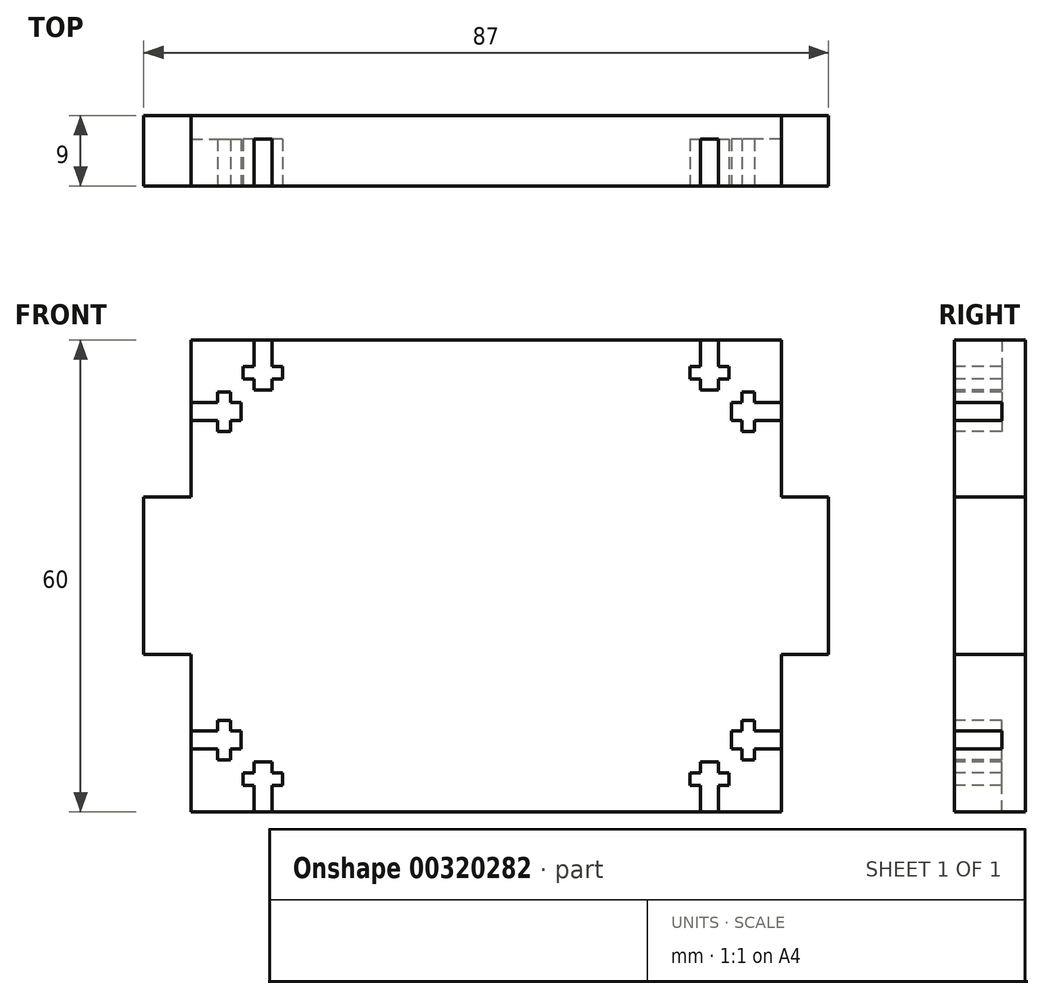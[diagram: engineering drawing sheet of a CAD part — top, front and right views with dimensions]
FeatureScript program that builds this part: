
annotation { "Feature Type Name" : "Feature", "Feature Type Description" : "" }
export const myFeature = defineFeature(function(context is Context, id is Id, definition is map)
    precondition{}
    {
        {
            var Q0;
            Q0=qCreatedBy(makeId("Front.planeOp"),FACE);
            var sketch = newSketch(context, id + "F0", { "sketchPlane" : qUnion([Q0])});
            skLineSegment(sketch, "E0.bottom", {"start": v(-37.5, -30) * mm, "end": v(37.5, -30) * mm});
            skLineSegment(sketch, "E0.top", {"start": v(-37.5, 30) * mm, "end": v(37.5, 30) * mm});
            skLineSegment(sketch, "E0.left", {"start": v(-37.5, -30) * mm, "end": v(-37.5, 30) * mm});
            skLineSegment(sketch, "E0.right", {"start": v(37.5, -30) * mm, "end": v(37.5, 30) * mm});
            skPoint(sketch, "E0.middle", {"position": v(0, 0) * mm});
            skLineSegment(sketch, "E1", {"start": v(0, 30) * mm, "end": v(0, -30) * mm, "construction": true});
            skLineSegment(sketch, "E2", {"start": v(-37.5, 0) * mm, "end": v(37.5, 0) * mm, "construction": true});
            skLineSegment(sketch, "E3", {"start": v(-37.5, 10) * mm, "end": v(-43.5, 10) * mm});
            skLineSegment(sketch, "E4", {"start": v(-43.5, 10) * mm, "end": v(-43.5, -10) * mm});
            skLineSegment(sketch, "E5", {"start": v(-43.5, -10) * mm, "end": v(-37.5, -10) * mm});
            skLineSegment(sketch, "E6.MirrorCS", {"start": v(43.5, -10) * mm, "end": v(37.5, -10) * mm});
            skLineSegment(sketch, "E7.MirrorCS", {"start": v(37.5, 10) * mm, "end": v(43.5, 10) * mm});
            skLineSegment(sketch, "E8.MirrorCS", {"start": v(43.5, 10) * mm, "end": v(43.5, -10) * mm});
            skLineSegment(sketch, "E9.top", {"start": v(-27.21, -23.65) * mm, "end": v(-29.5, -23.65) * mm});
            skLineSegment(sketch, "E9.left", {"start": v(-27.21, -30) * mm, "end": v(-27.21, -26.6) * mm});
            skLineSegment(sketch, "E9.right", {"start": v(-29.5, -30) * mm, "end": v(-29.5, -26.6) * mm});
            skLineSegment(sketch, "E10.bottom", {"start": v(-25.86, -26.6) * mm, "end": v(-27.21, -26.6) * mm});
            skLineSegment(sketch, "E10.top", {"start": v(-25.86, -25) * mm, "end": v(-27.21, -25) * mm});
            skLineSegment(sketch, "E10.left", {"start": v(-25.86, -26.6) * mm, "end": v(-25.86, -25) * mm});
            skLineSegment(sketch, "E10.right", {"start": v(-30.86, -26.6) * mm, "end": v(-30.86, -25) * mm});
            skLineSegment(sketch, "E11.trimOffspring", {"start": v(-29.5, -25) * mm, "end": v(-29.5, -23.65) * mm});
            skLineSegment(sketch, "E12.trimOffspring", {"start": v(-29.5, -25) * mm, "end": v(-30.86, -25) * mm});
            skLineSegment(sketch, "E13.trimOffspring", {"start": v(-29.5, -26.6) * mm, "end": v(-30.86, -26.6) * mm});
            skLineSegment(sketch, "E14.trimOffspring", {"start": v(-27.21, -25) * mm, "end": v(-27.21, -23.65) * mm});
            skLineSegment(sketch, "E15.top", {"start": v(-31.15, -22) * mm, "end": v(-31.15, -19.71) * mm});
            skLineSegment(sketch, "E15.left", {"start": v(-37.5, -22) * mm, "end": v(-34.1, -22) * mm});
            skLineSegment(sketch, "E15.right", {"start": v(-37.5, -19.71) * mm, "end": v(-34.1, -19.71) * mm});
            skLineSegment(sketch, "E16.bottom", {"start": v(-34.1, -23.36) * mm, "end": v(-34.1, -22) * mm});
            skLineSegment(sketch, "E16.top", {"start": v(-32.5, -23.36) * mm, "end": v(-32.5, -22) * mm});
            skLineSegment(sketch, "E16.left", {"start": v(-34.1, -23.36) * mm, "end": v(-32.5, -23.36) * mm});
            skLineSegment(sketch, "E16.right", {"start": v(-34.1, -18.36) * mm, "end": v(-32.5, -18.36) * mm});
            skLineSegment(sketch, "E17.trimOffspring", {"start": v(-32.5, -19.71) * mm, "end": v(-31.15, -19.71) * mm});
            skLineSegment(sketch, "E18.trimOffspring", {"start": v(-32.5, -19.71) * mm, "end": v(-32.5, -18.36) * mm});
            skLineSegment(sketch, "E19.trimOffspring", {"start": v(-34.1, -19.71) * mm, "end": v(-34.1, -18.36) * mm});
            skLineSegment(sketch, "E20.trimOffspring", {"start": v(-32.5, -22) * mm, "end": v(-31.15, -22) * mm});
            skLineSegment(sketch, "E21.MirrorCS", {"start": v(29.5, -26.6) * mm, "end": v(30.86, -26.6) * mm});
            skLineSegment(sketch, "E22.MirrorCS", {"start": v(25.86, -26.6) * mm, "end": v(27.21, -26.6) * mm});
            skLineSegment(sketch, "E23.MirrorCS", {"start": v(29.5, -25) * mm, "end": v(29.5, -23.65) * mm});
            skLineSegment(sketch, "E24.MirrorCS", {"start": v(25.86, -25) * mm, "end": v(27.21, -25) * mm});
            skLineSegment(sketch, "E25.MirrorCS", {"start": v(32.5, -22) * mm, "end": v(31.15, -22) * mm});
            skLineSegment(sketch, "E26.MirrorCS", {"start": v(32.5, -19.71) * mm, "end": v(32.5, -18.36) * mm});
            skLineSegment(sketch, "E27.MirrorCS", {"start": v(32.5, -23.36) * mm, "end": v(32.5, -22) * mm});
            skLineSegment(sketch, "E28.MirrorCS", {"start": v(27.21, -25) * mm, "end": v(27.21, -23.65) * mm});
            skLineSegment(sketch, "E29.MirrorCS", {"start": v(32.5, -19.71) * mm, "end": v(31.15, -19.71) * mm});
            skLineSegment(sketch, "E30.MirrorCS", {"start": v(34.1, -23.36) * mm, "end": v(34.1, -22) * mm});
            skLineSegment(sketch, "E31.MirrorCS", {"start": v(34.1, -19.71) * mm, "end": v(34.1, -18.36) * mm});
            skLineSegment(sketch, "E32.MirrorCS", {"start": v(29.5, -25) * mm, "end": v(30.86, -25) * mm});
            skLineSegment(sketch, "E33.MirrorCS", {"start": v(37.5, -19.71) * mm, "end": v(34.1, -19.71) * mm});
            skLineSegment(sketch, "E34.MirrorCS", {"start": v(37.5, -22) * mm, "end": v(34.1, -22) * mm});
            skLineSegment(sketch, "E35.MirrorCS", {"start": v(34.1, -18.36) * mm, "end": v(32.5, -18.36) * mm});
            skLineSegment(sketch, "E36.MirrorCS", {"start": v(27.21, -30) * mm, "end": v(27.21, -26.6) * mm});
            skLineSegment(sketch, "E37.MirrorCS", {"start": v(29.5, -30) * mm, "end": v(29.5, -26.6) * mm});
            skLineSegment(sketch, "E38.MirrorCS", {"start": v(34.1, -23.36) * mm, "end": v(32.5, -23.36) * mm});
            skLineSegment(sketch, "E39.MirrorCS", {"start": v(30.86, -26.6) * mm, "end": v(30.86, -25) * mm});
            skLineSegment(sketch, "E40.MirrorCS", {"start": v(27.21, -23.65) * mm, "end": v(29.5, -23.65) * mm});
            skLineSegment(sketch, "E41.MirrorCS", {"start": v(31.15, -22) * mm, "end": v(31.15, -19.71) * mm});
            skLineSegment(sketch, "E42.MirrorCS", {"start": v(25.86, -26.6) * mm, "end": v(25.86, -25) * mm});
            skLineSegment(sketch, "E43.MirrorCS", {"start": v(-30.86, 26.6) * mm, "end": v(-30.86, 25) * mm});
            skLineSegment(sketch, "E44.MirrorCS", {"start": v(-27.21, 25) * mm, "end": v(-27.21, 23.65) * mm});
            skLineSegment(sketch, "E45.MirrorCS", {"start": v(29.5, 26.6) * mm, "end": v(30.86, 26.6) * mm});
            skLineSegment(sketch, "E46.MirrorCS", {"start": v(-29.5, 25) * mm, "end": v(-30.86, 25) * mm});
            skLineSegment(sketch, "E47.MirrorCS", {"start": v(-34.1, 18.36) * mm, "end": v(-32.5, 18.36) * mm});
            skLineSegment(sketch, "E48.MirrorCS", {"start": v(-25.86, 25) * mm, "end": v(-27.21, 25) * mm});
            skLineSegment(sketch, "E49.MirrorCS", {"start": v(27.21, 25) * mm, "end": v(27.21, 23.65) * mm});
            skLineSegment(sketch, "E50.MirrorCS", {"start": v(-32.5, 23.36) * mm, "end": v(-32.5, 22) * mm});
            skLineSegment(sketch, "E51.MirrorCS", {"start": v(-25.86, 26.6) * mm, "end": v(-27.21, 26.6) * mm});
            skLineSegment(sketch, "E52.MirrorCS", {"start": v(25.86, 25) * mm, "end": v(27.21, 25) * mm});
            skLineSegment(sketch, "E53.MirrorCS", {"start": v(32.5, 22) * mm, "end": v(31.15, 22) * mm});
            skLineSegment(sketch, "E54.MirrorCS", {"start": v(31.15, 22) * mm, "end": v(31.15, 19.71) * mm});
            skLineSegment(sketch, "E55.MirrorCS", {"start": v(-25.86, 26.6) * mm, "end": v(-25.86, 25) * mm});
            skLineSegment(sketch, "E56.MirrorCS", {"start": v(34.1, 23.36) * mm, "end": v(32.5, 23.36) * mm});
            skLineSegment(sketch, "E57.MirrorCS", {"start": v(-32.5, 22) * mm, "end": v(-31.15, 22) * mm});
            skLineSegment(sketch, "E58.MirrorCS", {"start": v(34.1, 19.71) * mm, "end": v(34.1, 18.36) * mm});
            skLineSegment(sketch, "E59.MirrorCS", {"start": v(29.5, 25) * mm, "end": v(29.5, 23.65) * mm});
            skLineSegment(sketch, "E60.MirrorCS", {"start": v(-29.5, 25) * mm, "end": v(-29.5, 23.65) * mm});
            skLineSegment(sketch, "E61.MirrorCS", {"start": v(29.5, 25) * mm, "end": v(30.86, 25) * mm});
            skLineSegment(sketch, "E62.MirrorCS", {"start": v(-34.1, 23.36) * mm, "end": v(-34.1, 22) * mm});
            skLineSegment(sketch, "E63.MirrorCS", {"start": v(25.86, 26.6) * mm, "end": v(27.21, 26.6) * mm});
            skLineSegment(sketch, "E64.MirrorCS", {"start": v(34.1, 18.36) * mm, "end": v(32.5, 18.36) * mm});
            skLineSegment(sketch, "E65.MirrorCS", {"start": v(-31.15, 22) * mm, "end": v(-31.15, 19.71) * mm});
            skLineSegment(sketch, "E66.MirrorCS", {"start": v(-32.5, 19.71) * mm, "end": v(-32.5, 18.36) * mm});
            skLineSegment(sketch, "E67.MirrorCS", {"start": v(32.5, 19.71) * mm, "end": v(31.15, 19.71) * mm});
            skLineSegment(sketch, "E68.MirrorCS", {"start": v(32.5, 19.71) * mm, "end": v(32.5, 18.36) * mm});
            skLineSegment(sketch, "E69.MirrorCS", {"start": v(25.86, 26.6) * mm, "end": v(25.86, 25) * mm});
            skLineSegment(sketch, "E70.MirrorCS", {"start": v(-32.5, 19.71) * mm, "end": v(-31.15, 19.71) * mm});
            skLineSegment(sketch, "E71.MirrorCS", {"start": v(-34.1, 23.36) * mm, "end": v(-32.5, 23.36) * mm});
            skLineSegment(sketch, "E72.MirrorCS", {"start": v(32.5, 23.36) * mm, "end": v(32.5, 22) * mm});
            skLineSegment(sketch, "E73.MirrorCS", {"start": v(-29.5, 26.6) * mm, "end": v(-30.86, 26.6) * mm});
            skLineSegment(sketch, "E74.MirrorCS", {"start": v(30.86, 26.6) * mm, "end": v(30.86, 25) * mm});
            skLineSegment(sketch, "E75.MirrorCS", {"start": v(-34.1, 19.71) * mm, "end": v(-34.1, 18.36) * mm});
            skLineSegment(sketch, "E76.MirrorCS", {"start": v(34.1, 23.36) * mm, "end": v(34.1, 22) * mm});
            skLineSegment(sketch, "E77.MirrorCS", {"start": v(-27.21, 23.65) * mm, "end": v(-29.5, 23.65) * mm});
            skLineSegment(sketch, "E78.MirrorCS", {"start": v(27.21, 30) * mm, "end": v(27.21, 26.6) * mm});
            skLineSegment(sketch, "E79.MirrorCS", {"start": v(37.5, 19.71) * mm, "end": v(34.1, 19.71) * mm});
            skLineSegment(sketch, "E80.MirrorCS", {"start": v(-37.5, 22) * mm, "end": v(-34.1, 22) * mm});
            skLineSegment(sketch, "E81.MirrorCS", {"start": v(29.5, 30) * mm, "end": v(29.5, 26.6) * mm});
            skLineSegment(sketch, "E82.MirrorCS", {"start": v(27.21, 23.65) * mm, "end": v(29.5, 23.65) * mm});
            skLineSegment(sketch, "E83.MirrorCS", {"start": v(37.5, 22) * mm, "end": v(34.1, 22) * mm});
            skLineSegment(sketch, "E84.MirrorCS", {"start": v(-27.21, 30) * mm, "end": v(-27.21, 26.6) * mm});
            skLineSegment(sketch, "E85.MirrorCS", {"start": v(-29.5, 30) * mm, "end": v(-29.5, 26.6) * mm});
            skLineSegment(sketch, "E86.MirrorCS", {"start": v(-37.5, 19.71) * mm, "end": v(-34.1, 19.71) * mm});
            skSolve(sketch);
        }
        {
            var Q0;
            Q0 = qSketchRegion(id + "F0", true);
            extrude(context, id + "F1", {"entities" : qUnion([Q0]), "oppositeDirection" : true, "depth" : 9 * mm});
        }
        {
            var Q0;
            Q0=makeQuery(id+"F0.imprint","IMPRINT",FACE,{"disambiguationData":[TD([[makeQuery(id+"F0.imprint","IMPRINT",EDGE,{"derivedFrom":sQuery(id+"F0.wireOp",EDGE,"E47.MirrorCS")}),1.0]])]});
            var Q1;
            Q1=makeQuery(id+"F0.imprint","IMPRINT",FACE,{"disambiguationData":[TD([[makeQuery(id+"F0.imprint","IMPRINT",EDGE,{"derivedFrom":sQuery(id+"F0.wireOp",EDGE,"E43.MirrorCS")}),1.0]])]});
            var Q2;
            Q2=makeQuery(id+"F0.imprint","IMPRINT",FACE,{"disambiguationData":[TD([[makeQuery(id+"F0.imprint","IMPRINT",EDGE,{"derivedFrom":sQuery(id+"F0.wireOp",EDGE,"E15.top")}),1.0]])]});
            var Q3;
            Q3=makeQuery(id+"F0.imprint","IMPRINT",FACE,{"disambiguationData":[TD([[makeQuery(id+"F0.imprint","IMPRINT",EDGE,{"derivedFrom":sQuery(id+"F0.wireOp",EDGE,"E9.top")}),1.0]])]});
            var Q4;
            Q4=makeQuery(id+"F0.imprint","IMPRINT",FACE,{"disambiguationData":[TD([[makeQuery(id+"F0.imprint","IMPRINT",EDGE,{"derivedFrom":sQuery(id+"F0.wireOp",EDGE,"E21.MirrorCS")}),1.0]])]});
            var Q5;
            Q5=makeQuery(id+"F0.imprint","IMPRINT",FACE,{"disambiguationData":[TD([[makeQuery(id+"F0.imprint","IMPRINT",EDGE,{"derivedFrom":sQuery(id+"F0.wireOp",EDGE,"E25.MirrorCS")}),-1.0]])]});
            var Q6;
            Q6=makeQuery(id+"F0.imprint","IMPRINT",FACE,{"disambiguationData":[TD([[makeQuery(id+"F0.imprint","IMPRINT",EDGE,{"derivedFrom":sQuery(id+"F0.wireOp",EDGE,"E53.MirrorCS")}),1.0]])]});
            var Q7;
            Q7=makeQuery(id+"F0.imprint","IMPRINT",FACE,{"disambiguationData":[TD([[makeQuery(id+"F0.imprint","IMPRINT",EDGE,{"derivedFrom":sQuery(id+"F0.wireOp",EDGE,"E45.MirrorCS")}),-1.0]])]});
            extrude(context, id + "F2", {"entities" : qUnion([Q0, Q1, Q2, Q3, Q4, Q5, Q6, Q7]), "operationType" : NewBodyOperationType.REMOVE, "oppositeDirection" : true, "depth" : 6 * mm});
        }
    });
